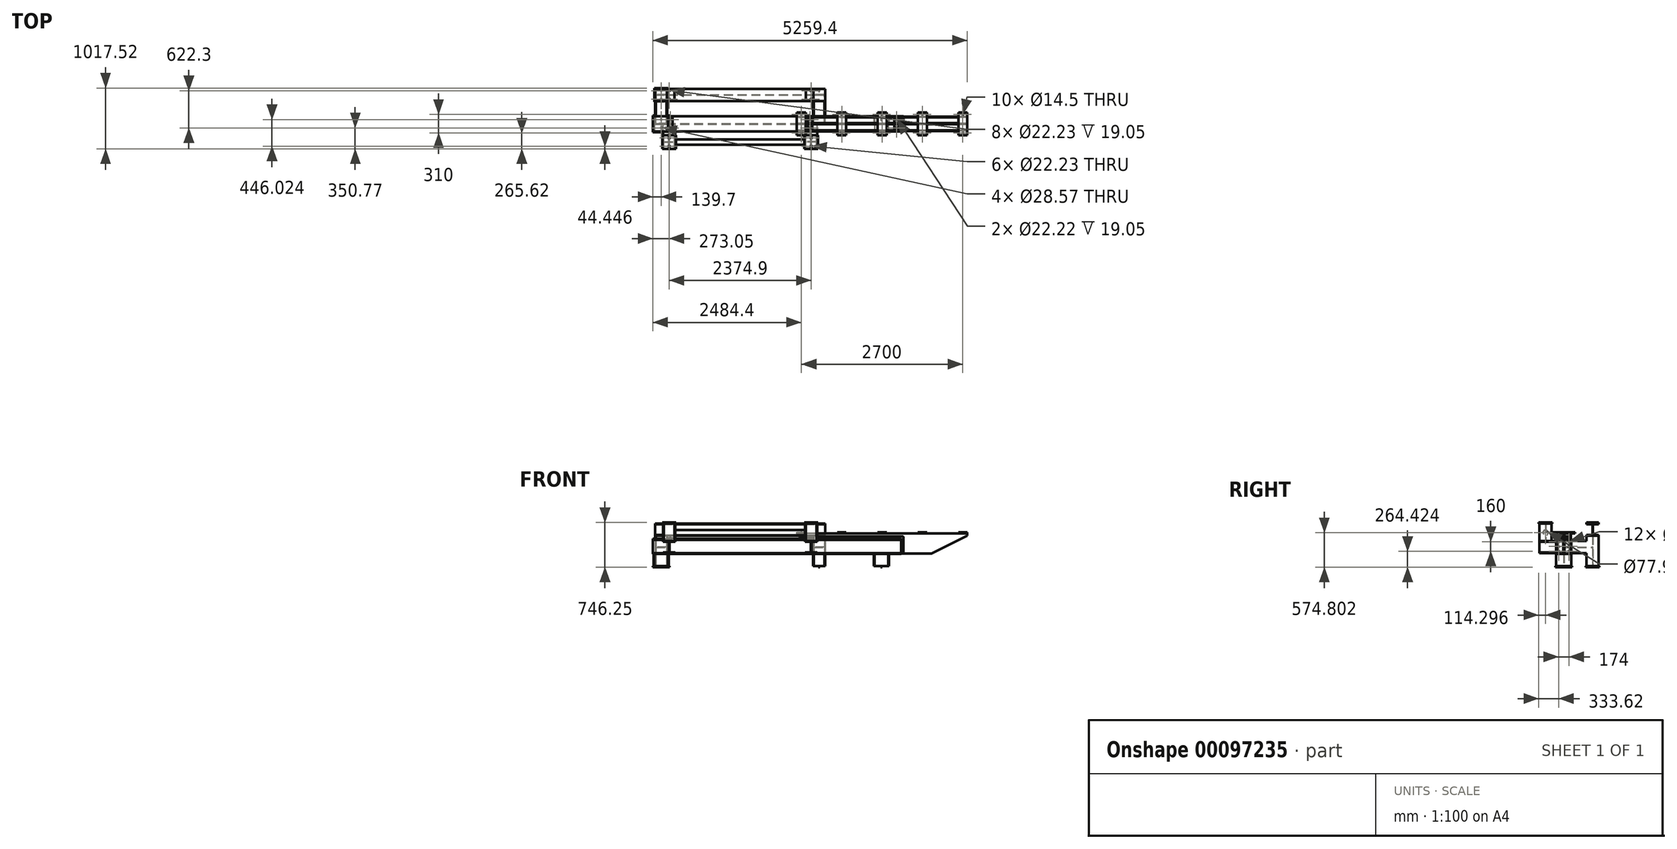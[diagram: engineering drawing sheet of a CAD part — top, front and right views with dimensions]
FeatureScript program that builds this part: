
annotation { "Feature Type Name" : "Feature", "Feature Type Description" : "" }
export const myFeature = defineFeature(function(context is Context, id is Id, definition is map)
    precondition{}
    {
        {
            var Q0;
            Q0=qCreatedBy(makeId("Top.planeOp"),FACE);
            var sketch = newSketch(context, id + "F0", { "sketchPlane" : qUnion([Q0])});
            skLineSegment(sketch, "E0.bottom", {"start": v(-1320.8, 241.3) * mm, "end": v(1320.8, 241.3) * mm, "construction": true});
            skLineSegment(sketch, "E0.top", {"start": v(-1320.8, -241.3) * mm, "end": v(1320.8, -241.3) * mm, "construction": true});
            skLineSegment(sketch, "E0.left", {"start": v(-1320.8, 241.3) * mm, "end": v(-1320.8, -241.3) * mm, "construction": true});
            skLineSegment(sketch, "E0.right", {"start": v(1320.8, 241.3) * mm, "end": v(1320.8, -241.3) * mm, "construction": true});
            skPoint(sketch, "E0.middle", {"position": v(0, 0) * mm});
            skLineSegment(sketch, "E1.bottom", {"start": v(-1435.1, 355.6) * mm, "end": v(-1206.5, 355.6) * mm});
            skLineSegment(sketch, "E1.top", {"start": v(-1435.1, 127) * mm, "end": v(-1206.5, 127) * mm});
            skLineSegment(sketch, "E1.left", {"start": v(-1435.1, 355.6) * mm, "end": v(-1435.1, 127) * mm});
            skLineSegment(sketch, "E1.right", {"start": v(-1206.5, 355.6) * mm, "end": v(-1206.5, 127) * mm});
            skPoint(sketch, "E1.middle", {"position": v(-1320.8, 241.3) * mm});
            skLineSegment(sketch, "E2", {"start": v(0, -413.23) * mm, "end": v(0, 639.03) * mm, "construction": true});
            skLineSegment(sketch, "E3", {"start": v(-1320.8, 355.6) * mm, "end": v(-1320.8, 127) * mm, "construction": true});
            skLineSegment(sketch, "E4", {"start": v(-1435.1, 241.3) * mm, "end": v(-1206.5, 241.3) * mm, "construction": true});
            skLineSegment(sketch, "E5.0", {"start": v(-1435.1, 311.15) * mm, "end": v(-1206.5, 311.15) * mm, "construction": true});
            skCircle(sketch, "E6", {"center": v(-1320.8, 311.15) * mm, "radius": 14.29 * mm});
            skCircle(sketch, "E7.MirrorC", {"center": v(-1320.8, 171.45) * mm, "radius": 14.29 * mm});
            skCircle(sketch, "E8.MirrorC", {"center": v(1320.8, 311.15) * mm, "radius": 14.29 * mm});
            skCircle(sketch, "E9.MirrorC", {"center": v(1320.8, 171.45) * mm, "radius": 14.29 * mm});
            skLineSegment(sketch, "E10.MirrorCS", {"start": v(1435.1, 311.15) * mm, "end": v(1206.5, 311.15) * mm, "construction": true});
            skLineSegment(sketch, "E11.MirrorCS", {"start": v(1435.1, 241.3) * mm, "end": v(1206.5, 241.3) * mm, "construction": true});
            skLineSegment(sketch, "E12.MirrorCS", {"start": v(1320.8, 355.6) * mm, "end": v(1320.8, 127) * mm, "construction": true});
            skLineSegment(sketch, "E13.MirrorCS", {"start": v(1435.1, 355.6) * mm, "end": v(1206.5, 355.6) * mm});
            skPoint(sketch, "E14.MirrorP", {"position": v(1320.8, 241.3) * mm});
            skLineSegment(sketch, "E15.MirrorCS", {"start": v(1206.5, 355.6) * mm, "end": v(1206.5, 127) * mm});
            skLineSegment(sketch, "E16.MirrorCS", {"start": v(1435.1, 127) * mm, "end": v(1206.5, 127) * mm});
            skLineSegment(sketch, "E17.MirrorCS", {"start": v(1435.1, 355.6) * mm, "end": v(1435.1, 127) * mm});
            skLineSegment(sketch, "E18.bottom", {"start": v(-1460.5, -381) * mm, "end": v(-1181.1, -381) * mm});
            skLineSegment(sketch, "E18.top", {"start": v(-1460.5, -101.6) * mm, "end": v(-1181.1, -101.6) * mm});
            skLineSegment(sketch, "E18.left", {"start": v(-1460.5, -381) * mm, "end": v(-1460.5, -101.6) * mm});
            skLineSegment(sketch, "E18.right", {"start": v(-1181.1, -381) * mm, "end": v(-1181.1, -101.6) * mm});
            skPoint(sketch, "E18.middle", {"position": v(-1320.8, -241.3) * mm});
            skLineSegment(sketch, "E19", {"start": v(-1320.8, -241.3) * mm, "end": v(-1460.5, -241.3) * mm, "construction": true});
            skLineSegment(sketch, "E20.0", {"start": v(-1320.8, -171.45) * mm, "end": v(-1460.5, -171.45) * mm, "construction": true});
            skCircle(sketch, "E21", {"center": v(-1320.8, -171.45) * mm, "radius": 14.29 * mm});
            skCircle(sketch, "E22.MirrorC", {"center": v(-1320.8, -311.15) * mm, "radius": 14.29 * mm});
            skLineSegment(sketch, "E23", {"start": v(-1320.8, -638.8) * mm, "end": v(-1320.8, -1011) * mm, "construction": true});
            skPoint(sketch, "E24.orphan", {"position": v(-1320.8, -381) * mm});
            skLineSegment(sketch, "E25.0", {"start": v(0, -638.8) * mm, "end": v(0, -1011) * mm, "construction": true});
            skLineSegment(sketch, "E26.0", {"start": v(1320.8, -638.8) * mm, "end": v(1320.8, -1011) * mm, "construction": true});
            skLineSegment(sketch, "E27.0", {"start": v(2362.2, -638.8) * mm, "end": v(2362.2, -1011) * mm, "construction": true});
            skLineSegment(sketch, "E28", {"start": v(-1320.8, -1011) * mm, "end": v(2362.2, -1011) * mm, "construction": true});
            skLineSegment(sketch, "E29", {"start": v(520.7, -1011) * mm, "end": v(520.7, -1354.57) * mm, "construction": true});
            skCircle(sketch, "E30.MirrorC", {"center": v(2362.2, -171.45) * mm, "radius": 14.29 * mm});
            skCircle(sketch, "E31.MirrorC", {"center": v(2362.2, -311.15) * mm, "radius": 14.29 * mm});
            skLineSegment(sketch, "E32.MirrorCS", {"start": v(2362.2, -171.45) * mm, "end": v(2501.9, -171.45) * mm, "construction": true});
            skLineSegment(sketch, "E33.MirrorCS", {"start": v(2501.9, -101.6) * mm, "end": v(2222.5, -101.6) * mm});
            skLineSegment(sketch, "E34.MirrorCS", {"start": v(2501.9, -381) * mm, "end": v(2222.5, -381) * mm});
            skLineSegment(sketch, "E35.MirrorCS", {"start": v(2362.2, -241.3) * mm, "end": v(2501.9, -241.3) * mm, "construction": true});
            skPoint(sketch, "E36.MirrorP", {"position": v(2362.2, -241.3) * mm});
            skLineSegment(sketch, "E37.MirrorCS", {"start": v(2222.5, -381) * mm, "end": v(2222.5, -101.6) * mm});
            skPoint(sketch, "E38.MirrorP", {"position": v(2362.2, -381) * mm});
            skLineSegment(sketch, "E39.MirrorCS", {"start": v(2501.9, -381) * mm, "end": v(2501.9, -101.6) * mm});
            skSolve(sketch);
        }
        {
            var Q0;
            Q0=makeQuery(id+"F0.imprint","IMPRINT",FACE,{"disambiguationData":[TD([[makeQuery(id+"F0.imprint","IMPRINT",EDGE,{"derivedFrom":sQuery(id+"F0.wireOp",EDGE,"E1.bottom")}),-1.0]])]});
            var Q1;
            Q1=makeQuery(id+"F0.imprint","IMPRINT",FACE,{"disambiguationData":[TD([[makeQuery(id+"F0.imprint","IMPRINT",EDGE,{"derivedFrom":sQuery(id+"F0.wireOp",EDGE,"E8.MirrorC")}),1.0]])]});
            var Q2;
            Q2=makeQuery(id+"F0.imprint","IMPRINT",FACE,{"disambiguationData":[TD([[makeQuery(id+"F0.imprint","IMPRINT",EDGE,{"derivedFrom":sQuery(id+"F0.wireOp",EDGE,"E30.MirrorC")}),1.0]])]});
            var Q3;
            Q3=makeQuery(id+"F0.imprint","IMPRINT",FACE,{"disambiguationData":[TD([[makeQuery(id+"F0.imprint","IMPRINT",EDGE,{"derivedFrom":sQuery(id+"F0.wireOp",EDGE,"E18.bottom")}),1.0]])]});
            extrude(context, id + "F1", {"entities" : qUnion([Q0, Q1, Q2, Q3]), "depth" : 19.05 * mm});
        }
        {
            var Q0;
            Q0=makeQuery(id+"F1.opExtrude","CAP_FACE",FACE,{"disambiguationData":[OSD([sQuery(id+"F0.wireOp",EDGE,"E1.bottom"),sQuery(id+"F0.wireOp",EDGE,"E1.top"),sQuery(id+"F0.wireOp",EDGE,"E1.left"),sQuery(id+"F0.wireOp",EDGE,"E1.right"),sQuery(id+"F0.wireOp",EDGE,"E6"),sQuery(id+"F0.wireOp",EDGE,"E7.MirrorC")])],"isStart":false});
            var sketch = newSketch(context, id + "F2", { "sketchPlane" : qUnion([Q0])});
            skLineSegment(sketch, "E40.0", {"start": v(-1435.1, 241.3) * mm, "end": v(-1206.5, 241.3) * mm, "construction": true});
            skLineSegment(sketch, "E41.0", {"start": v(-1320.8, 355.6) * mm, "end": v(-1320.8, 127) * mm, "construction": true});
            skLineSegment(sketch, "E42.bottom", {"start": v(-1422.4, 342.9) * mm, "end": v(-1411.35, 342.9) * mm});
            skLineSegment(sketch, "E42.top", {"start": v(-1422.4, 139.7) * mm, "end": v(-1411.35, 139.7) * mm});
            skLineSegment(sketch, "E42.left", {"start": v(-1422.4, 342.9) * mm, "end": v(-1422.4, 139.7) * mm});
            skLineSegment(sketch, "E42.right", {"start": v(-1219.2, 342.9) * mm, "end": v(-1219.2, 139.7) * mm, "construction": true});
            skPoint(sketch, "E42.middle", {"position": v(-1320.8, 241.3) * mm});
            skLineSegment(sketch, "E43.0", {"start": v(-1411.35, 342.9) * mm, "end": v(-1411.35, 251.27) * mm});
            skLineSegment(sketch, "E44.trimOffspring", {"start": v(-1405, 237.68) * mm, "end": v(-1320.8, 237.68) * mm});
            skLineSegment(sketch, "E45.MirrorCS", {"start": v(-1405, 244.92) * mm, "end": v(-1320.8, 244.92) * mm});
            skLineSegment(sketch, "E46.trimOffspring", {"start": v(-1411.35, 231.33) * mm, "end": v(-1411.35, 139.7) * mm});
            skPoint(sketch, "E47.visualSharp", {"position": v(-1411.35, 244.92) * mm});
            skArc(sketch, "E47.filletArc", {"start": v(-1411.35, 251.27) * mm, "mid": v(-1409.5, 246.78) * mm, "end": v(-1405, 244.92) * mm});
            skPoint(sketch, "E48.visualSharp", {"position": v(-1411.35, 237.68) * mm});
            skArc(sketch, "E48.filletArc", {"start": v(-1405, 237.68) * mm, "mid": v(-1409.5, 235.82) * mm, "end": v(-1411.35, 231.33) * mm});
            skArc(sketch, "E49.MirrorCS", {"start": v(-1236.6, 237.68) * mm, "mid": v(-1232.1, 235.82) * mm, "end": v(-1230.25, 231.33) * mm});
            skArc(sketch, "E50.MirrorCS", {"start": v(-1230.25, 251.27) * mm, "mid": v(-1232.1, 246.78) * mm, "end": v(-1236.6, 244.92) * mm});
            skPoint(sketch, "E51.MirrorP", {"position": v(-1230.25, 237.68) * mm});
            skPoint(sketch, "E52.MirrorP", {"position": v(-1230.25, 244.92) * mm});
            skLineSegment(sketch, "E53.MirrorCS", {"start": v(-1230.25, 342.9) * mm, "end": v(-1230.25, 251.27) * mm});
            skLineSegment(sketch, "E54.MirrorCS", {"start": v(-1236.6, 237.68) * mm, "end": v(-1320.8, 237.68) * mm});
            skLineSegment(sketch, "E55.MirrorCS", {"start": v(-1236.6, 244.92) * mm, "end": v(-1320.8, 244.92) * mm});
            skLineSegment(sketch, "E56.MirrorCS", {"start": v(-1219.2, 139.7) * mm, "end": v(-1230.25, 139.7) * mm});
            skLineSegment(sketch, "E57.MirrorCS", {"start": v(-1230.25, 231.33) * mm, "end": v(-1230.25, 139.7) * mm});
            skLineSegment(sketch, "E58.MirrorCS", {"start": v(-1219.2, 342.9) * mm, "end": v(-1230.25, 342.9) * mm});
            skLineSegment(sketch, "E59.MirrorCS", {"start": v(-1219.2, 342.9) * mm, "end": v(-1219.2, 139.7) * mm});
            skLineSegment(sketch, "E60.0", {"start": v(0, -413.23) * mm, "end": v(0, 639.03) * mm, "construction": true});
            skArc(sketch, "E61.MirrorCS", {"start": v(1411.35, 251.27) * mm, "mid": v(1409.5, 246.78) * mm, "end": v(1405, 244.92) * mm});
            skArc(sketch, "E62.MirrorCS", {"start": v(1405, 237.68) * mm, "mid": v(1409.5, 235.82) * mm, "end": v(1411.35, 231.33) * mm});
            skLineSegment(sketch, "E63.MirrorCS", {"start": v(1236.6, 244.92) * mm, "end": v(1320.8, 244.92) * mm});
            skArc(sketch, "E64.MirrorCS", {"start": v(1236.6, 237.68) * mm, "mid": v(1232.1, 235.82) * mm, "end": v(1230.25, 231.33) * mm});
            skLineSegment(sketch, "E65.MirrorCS", {"start": v(1422.4, 139.7) * mm, "end": v(1411.35, 139.7) * mm});
            skLineSegment(sketch, "E66.MirrorCS", {"start": v(1422.4, 342.9) * mm, "end": v(1411.35, 342.9) * mm});
            skArc(sketch, "E67.MirrorCS", {"start": v(1230.25, 251.27) * mm, "mid": v(1232.1, 246.78) * mm, "end": v(1236.6, 244.92) * mm});
            skLineSegment(sketch, "E68.MirrorCS", {"start": v(1236.6, 237.68) * mm, "end": v(1320.8, 237.68) * mm});
            skLineSegment(sketch, "E69.MirrorCS", {"start": v(1435.1, 241.3) * mm, "end": v(1206.5, 241.3) * mm, "construction": true});
            skLineSegment(sketch, "E70.MirrorCS", {"start": v(1405, 237.68) * mm, "end": v(1320.8, 237.68) * mm});
            skLineSegment(sketch, "E71.MirrorCS", {"start": v(1219.2, 342.9) * mm, "end": v(1230.25, 342.9) * mm});
            skLineSegment(sketch, "E72.MirrorCS", {"start": v(1219.2, 139.7) * mm, "end": v(1230.25, 139.7) * mm});
            skLineSegment(sketch, "E73.MirrorCS", {"start": v(1411.35, 342.9) * mm, "end": v(1411.35, 251.27) * mm});
            skLineSegment(sketch, "E74.MirrorCS", {"start": v(1405, 244.92) * mm, "end": v(1320.8, 244.92) * mm});
            skLineSegment(sketch, "E75.MirrorCS", {"start": v(1411.35, 231.33) * mm, "end": v(1411.35, 139.7) * mm});
            skPoint(sketch, "E76.MirrorP", {"position": v(1411.35, 237.68) * mm});
            skPoint(sketch, "E77.MirrorP", {"position": v(1320.8, 241.3) * mm});
            skLineSegment(sketch, "E78.MirrorCS", {"start": v(1219.2, 342.9) * mm, "end": v(1219.2, 139.7) * mm, "construction": true});
            skLineSegment(sketch, "E79.MirrorCS", {"start": v(1422.4, 342.9) * mm, "end": v(1422.4, 139.7) * mm});
            skPoint(sketch, "E80.MirrorP", {"position": v(1230.25, 237.68) * mm});
            skLineSegment(sketch, "E81.MirrorCS", {"start": v(1320.8, 355.6) * mm, "end": v(1320.8, 127) * mm, "construction": true});
            skPoint(sketch, "E82.MirrorP", {"position": v(1411.35, 244.92) * mm});
            skLineSegment(sketch, "E83.MirrorCS", {"start": v(1219.2, 342.9) * mm, "end": v(1219.2, 139.7) * mm});
            skLineSegment(sketch, "E84.MirrorCS", {"start": v(1230.25, 231.33) * mm, "end": v(1230.25, 139.7) * mm});
            skLineSegment(sketch, "E85.MirrorCS", {"start": v(1230.25, 342.9) * mm, "end": v(1230.25, 251.27) * mm});
            skPoint(sketch, "E86.MirrorP", {"position": v(1230.25, 244.92) * mm});
            skSolve(sketch);
        }
        {
            var Q0;
            Q0=qSketchRegion(id+"F2",true);
            extrude(context, id + "F3", {"entities" : qUnion([Q0]), "depth" : 504.95 * mm});
        }
        {
            var Q0;
            Q0=makeQuery(id+"F3.opExtrude","SWEPT_FACE",FACE,{"disambiguationData":[OSD([sQuery(id+"F2.wireOp",EDGE,"E79.MirrorCS")])]});
            var sketch = newSketch(context, id + "F4", { "sketchPlane" : qUnion([Q0])});
            skLineSegment(sketch, "E87.bottom", {"start": v(139.7, 524) * mm, "end": v(342.9, 524) * mm});
            skLineSegment(sketch, "E87.top", {"start": v(139.7, 727.2) * mm, "end": v(342.9, 727.2) * mm});
            skLineSegment(sketch, "E87.left", {"start": v(139.7, 524) * mm, "end": v(139.7, 535.05) * mm});
            skLineSegment(sketch, "E87.right", {"start": v(342.9, 524) * mm, "end": v(342.9, 535.05) * mm});
            skLineSegment(sketch, "E88", {"start": v(241.3, 727.2) * mm, "end": v(241.3, 524) * mm, "construction": true});
            skLineSegment(sketch, "E89.0", {"start": v(237.68, 709.8) * mm, "end": v(237.68, 541.4) * mm});
            skLineSegment(sketch, "E90.MirrorCS", {"start": v(244.92, 709.8) * mm, "end": v(244.92, 541.4) * mm});
            skLineSegment(sketch, "E91.0", {"start": v(139.7, 716.15) * mm, "end": v(231.33, 716.15) * mm});
            skLineSegment(sketch, "E92.0", {"start": v(139.7, 535.05) * mm, "end": v(231.33, 535.05) * mm});
            skLineSegment(sketch, "E93.trimOffspring", {"start": v(251.27, 716.15) * mm, "end": v(342.9, 716.15) * mm});
            skLineSegment(sketch, "E94.trimOffspring", {"start": v(251.27, 535.05) * mm, "end": v(342.9, 535.05) * mm});
            skLineSegment(sketch, "E95.trimOffspring", {"start": v(139.7, 716.15) * mm, "end": v(139.7, 727.2) * mm});
            skLineSegment(sketch, "E96.trimOffspring", {"start": v(342.9, 716.15) * mm, "end": v(342.9, 727.2) * mm});
            skPoint(sketch, "E97.newPointB", {"position": v(237.68, 524) * mm});
            skArc(sketch, "E97.filletArc", {"start": v(231.33, 535.05) * mm, "mid": v(235.82, 536.91) * mm, "end": v(237.68, 541.4) * mm});
            skPoint(sketch, "E98.newPointA", {"position": v(244.92, 524) * mm});
            skArc(sketch, "E98.filletArc", {"start": v(244.92, 541.4) * mm, "mid": v(246.78, 536.91) * mm, "end": v(251.27, 535.05) * mm});
            skPoint(sketch, "E99.newPointA", {"position": v(237.68, 727.2) * mm});
            skArc(sketch, "E99.filletArc", {"start": v(237.68, 709.8) * mm, "mid": v(235.82, 714.3) * mm, "end": v(231.33, 716.15) * mm});
            skPoint(sketch, "E100.newPointA", {"position": v(244.92, 727.2) * mm});
            skArc(sketch, "E100.filletArc", {"start": v(251.27, 716.15) * mm, "mid": v(246.78, 714.3) * mm, "end": v(244.92, 709.8) * mm});
            skSolve(sketch);
        }
        {
            var Q0;
            Q0=qSketchRegion(id+"F4",true);
            var Q1;
            Q1=makeQuery(id+"F3.opExtrude","SWEPT_FACE",FACE,{"disambiguationData":[OSD([sQuery(id+"F2.wireOp",EDGE,"E42.left")])]});
            extrude(context, id + "F5", {"entities" : qUnion([Q0]), "endBound" : BoundingType.UP_TO_SURFACE, "oppositeDirection" : true, "endBoundEntityFace" : qUnion([Q1]), "depth" : 25.4 * mm});
        }
        {
            var Q0;
            Q0=makeQuery(id+"F5.opExtrude","SWEPT_FACE",FACE,{"disambiguationData":[OSD([sQuery(id+"F4.wireOp",EDGE,"E87.top")])]});
            var sketch = newSketch(context, id + "F6", { "sketchPlane" : qUnion([Q0])});
            skLineSegment(sketch, "E101.0", {"start": v(0, -413.23) * mm, "end": v(0, 639.03) * mm, "construction": true});
            skLineSegment(sketch, "E102.0", {"start": v(-1187.45, -413.23) * mm, "end": v(-1187.45, 639.03) * mm, "construction": true});
            skLineSegment(sketch, "E103.0", {"start": v(-1225.55, 139.7) * mm, "end": v(-1225.55, 342.9) * mm});
            skLineSegment(sketch, "E104.0", {"start": v(-1098.55, 139.7) * mm, "end": v(-1098.55, 342.9) * mm});
            skLineSegment(sketch, "E105.0", {"start": v(-1422.4, 342.9) * mm, "end": v(1422.4, 342.9) * mm, "construction": true});
            skLineSegment(sketch, "E106.0.0", {"start": v(1225.55, 342.9) * mm, "end": v(-1225.55, 342.9) * mm});
            skLineSegment(sketch, "E106.0.1", {"start": v(-1422.4, 342.9) * mm, "end": v(-1422.4, 139.7) * mm});
            skLineSegment(sketch, "E106.0.2", {"start": v(-1225.55, 139.7) * mm, "end": v(-1098.55, 139.7) * mm});
            skLineSegment(sketch, "E106.0.3", {"start": v(1422.4, 139.7) * mm, "end": v(1422.4, 342.9) * mm});
            skLineSegment(sketch, "E107.trimOffspring", {"start": v(0, 139.7) * mm, "end": v(1225.55, 139.7) * mm});
            skLineSegment(sketch, "E108.0", {"start": v(-1320.8, 241.3) * mm, "end": v(1320.8, 241.3) * mm, "construction": true});
            skLineSegment(sketch, "E109.0", {"start": v(-1320.8, 311.15) * mm, "end": v(1320.8, 311.15) * mm, "construction": true});
            skCircle(sketch, "E110", {"center": v(-1187.45, 311.15) * mm, "radius": 11.11 * mm});
            skCircle(sketch, "E111.MirrorC", {"center": v(-1187.45, 171.45) * mm, "radius": 11.11 * mm});
            skCircle(sketch, "E112.MirrorC", {"center": v(1187.45, 311.15) * mm, "radius": 11.11 * mm});
            skCircle(sketch, "E113.MirrorC", {"center": v(1187.45, 171.45) * mm, "radius": 11.11 * mm});
            skLineSegment(sketch, "E114.MirrorCS", {"start": v(1225.55, 139.7) * mm, "end": v(1098.55, 139.7) * mm});
            skLineSegment(sketch, "E115.MirrorCS", {"start": v(1225.55, 139.7) * mm, "end": v(1225.55, 342.9) * mm});
            skLineSegment(sketch, "E116.MirrorCS", {"start": v(1098.55, 139.7) * mm, "end": v(1098.55, 342.9) * mm});
            skSolve(sketch);
        }
        {
            var Q0;
            Q0=qSketchRegion(id+"F6",true);
            extrude(context, id + "F7", {"entities" : qUnion([Q0]), "operationType" : NewBodyOperationType.ADD, "depth" : 19.05 * mm});
        }
        {
            var Q0;
            Q0=makeQuery(id+"F3.opExtrude","SWEPT_FACE",FACE,{"disambiguationData":[OSD([sQuery(id+"F2.wireOp",EDGE,"E44.trimOffspring"),sQuery(id+"F2.wireOp",EDGE,"E54.MirrorCS")])]});
            var sketch = newSketch(context, id + "F8", { "sketchPlane" : qUnion([Q0])});
            skLineSegment(sketch, "E117.0", {"start": v(-1460.5, 0) * mm, "end": v(-1181.1, 0) * mm, "construction": true});
            skLineSegment(sketch, "E118", {"start": v(-1320.8, 0) * mm, "end": v(-1320.8, 868.41) * mm, "construction": true});
            skLineSegment(sketch, "E119.0", {"start": v(-1422.4, 231.65) * mm, "end": v(-1411.35, 231.65) * mm});
            skLineSegment(sketch, "E120.0", {"start": v(-1422.4, 434.85) * mm, "end": v(-1411.35, 434.85) * mm});
            skLineSegment(sketch, "E121", {"start": v(-1422.4, 434.85) * mm, "end": v(-1422.4, 231.65) * mm});
            skLineSegment(sketch, "E122.0", {"start": v(-1411.35, 434.85) * mm, "end": v(-1411.35, 342.77) * mm});
            skLineSegment(sketch, "E123", {"start": v(-1411.35, 333.25) * mm, "end": v(-1320.8, 333.25) * mm, "construction": true});
            skLineSegment(sketch, "E124.0", {"start": v(-1405, 336.42) * mm, "end": v(-1320.8, 336.42) * mm});
            skLineSegment(sketch, "E125.MirrorCS", {"start": v(-1410.08, 330.07) * mm, "end": v(-1320.8, 330.07) * mm});
            skLineSegment(sketch, "E126.trimOffspring", {"start": v(-1411.35, 328.8) * mm, "end": v(-1411.35, 231.65) * mm});
            skPoint(sketch, "E127.newPointA", {"position": v(-1411.35, 336.42) * mm});
            skArc(sketch, "E127.filletArc", {"start": v(-1411.35, 342.77) * mm, "mid": v(-1409.5, 338.28) * mm, "end": v(-1405, 336.42) * mm});
            skPoint(sketch, "E128.visualSharp", {"position": v(-1411.35, 330.07) * mm});
            skArc(sketch, "E128.filletArc", {"start": v(-1410.08, 330.07) * mm, "mid": v(-1410.98, 329.7) * mm, "end": v(-1411.35, 328.8) * mm});
            skArc(sketch, "E129.MirrorCS", {"start": v(-1231.52, 330.07) * mm, "mid": v(-1230.62, 329.7) * mm, "end": v(-1230.25, 328.8) * mm});
            skArc(sketch, "E130.MirrorCS", {"start": v(-1230.25, 342.77) * mm, "mid": v(-1232.1, 338.28) * mm, "end": v(-1236.6, 336.42) * mm});
            skLineSegment(sketch, "E131.MirrorCS", {"start": v(-1219.2, 231.65) * mm, "end": v(-1230.25, 231.65) * mm});
            skLineSegment(sketch, "E132.MirrorCS", {"start": v(-1219.2, 434.85) * mm, "end": v(-1230.25, 434.85) * mm});
            skPoint(sketch, "E133.MirrorP", {"position": v(-1230.25, 336.42) * mm});
            skPoint(sketch, "E134.MirrorP", {"position": v(-1230.25, 330.07) * mm});
            skLineSegment(sketch, "E135.MirrorCS", {"start": v(-1230.25, 328.8) * mm, "end": v(-1230.25, 231.65) * mm});
            skLineSegment(sketch, "E136.MirrorCS", {"start": v(-1231.52, 330.07) * mm, "end": v(-1320.8, 330.07) * mm});
            skLineSegment(sketch, "E137.MirrorCS", {"start": v(-1219.2, 434.85) * mm, "end": v(-1219.2, 231.65) * mm});
            skLineSegment(sketch, "E138.MirrorCS", {"start": v(-1230.25, 434.85) * mm, "end": v(-1230.25, 342.77) * mm});
            skLineSegment(sketch, "E139.MirrorCS", {"start": v(-1230.25, 333.25) * mm, "end": v(-1320.8, 333.25) * mm, "construction": true});
            skLineSegment(sketch, "E140.MirrorCS", {"start": v(-1236.6, 336.42) * mm, "end": v(-1320.8, 336.42) * mm});
            skLineSegment(sketch, "E141", {"start": v(0, -179.83) * mm, "end": v(0, 965.66) * mm, "construction": true});
            skArc(sketch, "E142.MirrorCS", {"start": v(1411.35, 342.77) * mm, "mid": v(1409.5, 338.28) * mm, "end": v(1405, 336.42) * mm});
            skArc(sketch, "E143.MirrorCS", {"start": v(1410.08, 330.07) * mm, "mid": v(1410.98, 329.7) * mm, "end": v(1411.35, 328.8) * mm});
            skArc(sketch, "E144.MirrorCS", {"start": v(1230.25, 342.77) * mm, "mid": v(1232.1, 338.28) * mm, "end": v(1236.6, 336.42) * mm});
            skArc(sketch, "E145.MirrorCS", {"start": v(1231.52, 330.07) * mm, "mid": v(1230.62, 329.7) * mm, "end": v(1230.25, 328.8) * mm});
            skLineSegment(sketch, "E146.MirrorCS", {"start": v(1411.35, 333.25) * mm, "end": v(1320.8, 333.25) * mm, "construction": true});
            skLineSegment(sketch, "E147.MirrorCS", {"start": v(1219.2, 231.65) * mm, "end": v(1230.25, 231.65) * mm});
            skLineSegment(sketch, "E148.MirrorCS", {"start": v(1219.2, 434.85) * mm, "end": v(1230.25, 434.85) * mm});
            skLineSegment(sketch, "E149.MirrorCS", {"start": v(1422.4, 231.65) * mm, "end": v(1411.35, 231.65) * mm});
            skLineSegment(sketch, "E150.MirrorCS", {"start": v(1422.4, 434.85) * mm, "end": v(1411.35, 434.85) * mm});
            skLineSegment(sketch, "E151.MirrorCS", {"start": v(1405, 336.42) * mm, "end": v(1320.8, 336.42) * mm});
            skLineSegment(sketch, "E152.MirrorCS", {"start": v(1410.08, 330.07) * mm, "end": v(1320.8, 330.07) * mm});
            skLineSegment(sketch, "E153.MirrorCS", {"start": v(1230.25, 333.25) * mm, "end": v(1320.8, 333.25) * mm, "construction": true});
            skLineSegment(sketch, "E154.MirrorCS", {"start": v(1231.52, 330.07) * mm, "end": v(1320.8, 330.07) * mm});
            skLineSegment(sketch, "E155.MirrorCS", {"start": v(1236.6, 336.42) * mm, "end": v(1320.8, 336.42) * mm});
            skLineSegment(sketch, "E156.MirrorCS", {"start": v(1411.35, 328.8) * mm, "end": v(1411.35, 231.65) * mm});
            skPoint(sketch, "E157.MirrorP", {"position": v(1411.35, 330.07) * mm});
            skPoint(sketch, "E158.MirrorP", {"position": v(1411.35, 336.42) * mm});
            skLineSegment(sketch, "E159.MirrorCS", {"start": v(1422.4, 434.85) * mm, "end": v(1422.4, 231.65) * mm});
            skLineSegment(sketch, "E160.MirrorCS", {"start": v(1411.35, 434.85) * mm, "end": v(1411.35, 342.77) * mm});
            skLineSegment(sketch, "E161.MirrorCS", {"start": v(1230.25, 434.85) * mm, "end": v(1230.25, 342.77) * mm});
            skLineSegment(sketch, "E162.MirrorCS", {"start": v(1230.25, 328.8) * mm, "end": v(1230.25, 231.65) * mm});
            skPoint(sketch, "E163.MirrorP", {"position": v(1230.25, 330.07) * mm});
            skPoint(sketch, "E164.MirrorP", {"position": v(1230.25, 336.42) * mm});
            skLineSegment(sketch, "E165.MirrorCS", {"start": v(1219.2, 434.85) * mm, "end": v(1219.2, 231.65) * mm});
            skSolve(sketch);
        }
        {
            var Q0;
            Q0=qSketchRegion(id+"F8",true);
            extrude(context, id + "F9", {"entities" : qUnion([Q0]), "operationType" : NewBodyOperationType.ADD, "depth" : 482.6 * mm});
        }
        {
            var Q0;
            Q0=qCreatedBy(makeId("Right.planeOp"),FACE);
            cPlane(context, id + "F10", {"entities" : qUnion([Q0]), "cplaneType" : CPlaneType.OFFSET, "offset" : 2692.4 * mm, "width" : 152.4 * mm, "height" : 152.4 * mm});
        }
        {
            var Q0;
            Q0=qCreatedBy(id+"F10.planeOp",FACE);
            var sketch = newSketch(context, id + "F11", { "sketchPlane" : qUnion([Q0])});
            skLineSegment(sketch, "E166.0", {"start": v(-381, 19.05) * mm, "end": v(-101.6, 19.05) * mm, "construction": true});
            skLineSegment(sketch, "E167", {"start": v(-241.3, 19.05) * mm, "end": v(-241.3, 468.37) * mm, "construction": true});
            skLineSegment(sketch, "E168.0", {"start": v(-381, 217.42) * mm, "end": v(-101.6, 217.42) * mm, "construction": true});
            skLineSegment(sketch, "E169.bottom", {"start": v(-368.3, 217.42) * mm, "end": v(-114.3, 217.42) * mm});
            skLineSegment(sketch, "E169.top", {"start": v(-368.3, 471.42) * mm, "end": v(-114.3, 471.42) * mm});
            skLineSegment(sketch, "E169.left", {"start": v(-368.3, 217.42) * mm, "end": v(-368.3, 231.65) * mm});
            skLineSegment(sketch, "E169.right", {"start": v(-114.3, 217.42) * mm, "end": v(-114.3, 231.65) * mm});
            skLineSegment(sketch, "E170.0", {"start": v(-368.3, 457.2) * mm, "end": v(-254, 457.2) * mm});
            skLineSegment(sketch, "E171.0", {"start": v(-368.3, 231.65) * mm, "end": v(-254, 231.65) * mm});
            skLineSegment(sketch, "E172.0", {"start": v(-234.95, 238) * mm, "end": v(-234.95, 450.85) * mm});
            skLineSegment(sketch, "E173.MirrorCS", {"start": v(-247.65, 238) * mm, "end": v(-247.65, 450.85) * mm});
            skLineSegment(sketch, "E174.trimOffspring", {"start": v(-368.3, 457.2) * mm, "end": v(-368.3, 471.42) * mm});
            skLineSegment(sketch, "E175.trimOffspring", {"start": v(-114.3, 457.2) * mm, "end": v(-114.3, 471.42) * mm});
            skLineSegment(sketch, "E176.trimOffspring", {"start": v(-228.6, 457.2) * mm, "end": v(-114.3, 457.2) * mm});
            skLineSegment(sketch, "E177.trimOffspring", {"start": v(-228.6, 231.65) * mm, "end": v(-114.3, 231.65) * mm});
            skPoint(sketch, "E178.newPointB", {"position": v(-247.65, 468.37) * mm});
            skArc(sketch, "E178.filletArc", {"start": v(-247.65, 450.85) * mm, "mid": v(-249.5, 455.34) * mm, "end": v(-254, 457.2) * mm});
            skPoint(sketch, "E179.newPointB", {"position": v(-234.95, 468.37) * mm});
            skArc(sketch, "E179.filletArc", {"start": v(-228.6, 457.2) * mm, "mid": v(-233.1, 455.34) * mm, "end": v(-234.95, 450.85) * mm});
            skPoint(sketch, "E180.newPointB", {"position": v(-234.95, 19.05) * mm});
            skArc(sketch, "E180.filletArc", {"start": v(-234.95, 238) * mm, "mid": v(-233.1, 233.5) * mm, "end": v(-228.6, 231.65) * mm});
            skPoint(sketch, "E181.newPointA", {"position": v(-247.65, 19.05) * mm});
            skArc(sketch, "E181.filletArc", {"start": v(-254, 231.65) * mm, "mid": v(-249.5, 233.5) * mm, "end": v(-247.65, 238) * mm});
            skSolve(sketch);
        }
        {
            var Q0;
            Q0=qSketchRegion(id+"F11",true);
            extrude(context, id + "F12", {"entities" : qUnion([Q0]), "oppositeDirection" : true, "depth" : 4152.9 * mm});
        }
        {
            var Q0;
            Q0=makeQuery(id+"F1.opExtrude","CAP_FACE",FACE,{"disambiguationData":[OSD([sQuery(id+"F0.wireOp",EDGE,"E18.bottom"),sQuery(id+"F0.wireOp",EDGE,"E18.top"),sQuery(id+"F0.wireOp",EDGE,"E18.left"),sQuery(id+"F0.wireOp",EDGE,"E18.right"),sQuery(id+"F0.wireOp",EDGE,"E21"),sQuery(id+"F0.wireOp",EDGE,"E22.MirrorC")])],"isStart":false});
            var sketch = newSketch(context, id + "F13", { "sketchPlane" : qUnion([Q0])});
            skLineSegment(sketch, "E182.bottom", {"start": v(-1447.8, -114.3) * mm, "end": v(-1433.58, -114.3) * mm});
            skLineSegment(sketch, "E182.top", {"start": v(-1447.8, -368.3) * mm, "end": v(-1433.58, -368.3) * mm});
            skLineSegment(sketch, "E182.left", {"start": v(-1447.8, -114.3) * mm, "end": v(-1447.8, -368.3) * mm});
            skLineSegment(sketch, "E182.right", {"start": v(-1193.8, -114.3) * mm, "end": v(-1193.8, -368.3) * mm});
            skPoint(sketch, "E182.middle", {"position": v(-1320.8, -241.3) * mm});
            skLineSegment(sketch, "E183.0", {"start": v(-1433.58, -114.3) * mm, "end": v(-1433.58, -236.98) * mm});
            skLineSegment(sketch, "E184.0", {"start": v(-1208.02, -114.3) * mm, "end": v(-1208.02, -236.98) * mm});
            skLineSegment(sketch, "E185.trimOffspring", {"start": v(-1208.02, -114.3) * mm, "end": v(-1193.8, -114.3) * mm});
            skLineSegment(sketch, "E186.trimOffspring", {"start": v(-1208.02, -368.3) * mm, "end": v(-1193.8, -368.3) * mm});
            skLineSegment(sketch, "E187.0", {"start": v(-1208.02, -236.98) * mm, "end": v(-1433.58, -236.98) * mm});
            skLineSegment(sketch, "E188.MirrorCS", {"start": v(-1208.02, -245.62) * mm, "end": v(-1433.58, -245.62) * mm});
            skPoint(sketch, "E189.orphan", {"position": v(-1460.5, -236.98) * mm});
            skPoint(sketch, "E190.orphan", {"position": v(-1460.5, -245.62) * mm});
            skLineSegment(sketch, "E191.trimOffspring", {"start": v(-1433.58, -245.62) * mm, "end": v(-1433.58, -368.3) * mm});
            skPoint(sketch, "E192.orphan", {"position": v(-1320.8, -236.98) * mm});
            skPoint(sketch, "E193.orphan", {"position": v(-1320.8, -245.62) * mm});
            skLineSegment(sketch, "E194.trimOffspring", {"start": v(-1208.02, -245.62) * mm, "end": v(-1208.02, -368.3) * mm});
            skLineSegment(sketch, "E195.MirrorCS", {"start": v(2489.2, -368.3) * mm, "end": v(2474.98, -368.3) * mm});
            skLineSegment(sketch, "E196.MirrorCS", {"start": v(2489.2, -114.3) * mm, "end": v(2474.98, -114.3) * mm});
            skLineSegment(sketch, "E197.MirrorCS", {"start": v(2249.42, -368.3) * mm, "end": v(2235.2, -368.3) * mm});
            skLineSegment(sketch, "E198.MirrorCS", {"start": v(2249.42, -114.3) * mm, "end": v(2235.2, -114.3) * mm});
            skPoint(sketch, "E199.MirrorP", {"position": v(2362.2, -245.62) * mm});
            skPoint(sketch, "E200.MirrorP", {"position": v(2362.2, -236.98) * mm});
            skLineSegment(sketch, "E201.MirrorCS", {"start": v(2249.42, -245.62) * mm, "end": v(2474.98, -245.62) * mm});
            skPoint(sketch, "E202.MirrorP", {"position": v(2501.9, -236.98) * mm});
            skLineSegment(sketch, "E203.MirrorCS", {"start": v(2249.42, -236.98) * mm, "end": v(2474.98, -236.98) * mm});
            skPoint(sketch, "E204.MirrorP", {"position": v(2362.2, -241.3) * mm});
            skPoint(sketch, "E205.MirrorP", {"position": v(2501.9, -245.62) * mm});
            skLineSegment(sketch, "E206.MirrorCS", {"start": v(2249.42, -245.62) * mm, "end": v(2249.42, -368.3) * mm});
            skLineSegment(sketch, "E207.MirrorCS", {"start": v(2474.98, -245.62) * mm, "end": v(2474.98, -368.3) * mm});
            skLineSegment(sketch, "E208.MirrorCS", {"start": v(2249.42, -114.3) * mm, "end": v(2249.42, -236.98) * mm});
            skLineSegment(sketch, "E209.MirrorCS", {"start": v(2474.98, -114.3) * mm, "end": v(2474.98, -236.98) * mm});
            skLineSegment(sketch, "E210.MirrorCS", {"start": v(2235.2, -114.3) * mm, "end": v(2235.2, -368.3) * mm});
            skLineSegment(sketch, "E211.MirrorCS", {"start": v(2489.2, -114.3) * mm, "end": v(2489.2, -368.3) * mm});
            skSolve(sketch);
        }
        {
            var Q0;
            Q0=qSketchRegion(id+"F13",true);
            extrude(context, id + "F14", {"entities" : qUnion([Q0]), "depth" : 198.37 * mm});
        }
        {
            var Q0;
            Q0=makeQuery(id+"F12.opExtrude","SWEPT_FACE",FACE,{"disambiguationData":[OSD([sQuery(id+"F11.wireOp",EDGE,"E169.top")])]});
            var sketch = newSketch(context, id + "F15", { "sketchPlane" : qUnion([Q0])});
            skLineSegment(sketch, "E212.0", {"start": v(-1615.4, -241.3) * mm, "end": v(2831.5, -241.3) * mm, "construction": true});
            skLineSegment(sketch, "E213.0", {"start": v(0, -413.23) * mm, "end": v(0, 639.03) * mm, "construction": true});
            skPoint(sketch, "E214.orphan", {"position": v(-1320.8, -241.3) * mm});
            skLineSegment(sketch, "E215.0", {"start": v(-1168.4, -689.85) * mm, "end": v(-1168.4, 639.03) * mm, "construction": true});
            skLineSegment(sketch, "E216.0", {"start": v(-1130.3, -355.6) * mm, "end": v(-1130.3, -127) * mm});
            skLineSegment(sketch, "E217.0", {"start": v(-1206.5, -127) * mm, "end": v(-1130.3, -127) * mm});
            skLineSegment(sketch, "E218.0", {"start": v(-1615.4, -171.45) * mm, "end": v(2831.5, -171.45) * mm, "construction": true});
            skLineSegment(sketch, "E219.MirrorCS", {"start": v(-1206.5, -355.6) * mm, "end": v(-1130.3, -355.6) * mm});
            skLineSegment(sketch, "E220.MirrorCS", {"start": v(-1206.5, -355.6) * mm, "end": v(-1206.5, -127) * mm});
            skPoint(sketch, "E221.orphan", {"position": v(-1130.3, 639.03) * mm});
            skPoint(sketch, "E222.orphan", {"position": v(-1206.5, 639.03) * mm});
            skPoint(sketch, "E223.orphan", {"position": v(-1615.4, -127) * mm});
            skPoint(sketch, "E224.orphan", {"position": v(-1615.4, -355.6) * mm});
            skPoint(sketch, "E225.orphan", {"position": v(-1206.5, -689.85) * mm});
            skPoint(sketch, "E226.orphan", {"position": v(-1130.3, -689.85) * mm});
            skCircle(sketch, "E227", {"center": v(-1168.4, -171.45) * mm, "radius": 11.11 * mm});
            skCircle(sketch, "E228.MirrorC", {"center": v(-1168.4, -311.15) * mm, "radius": 11.11 * mm});
            skLineSegment(sketch, "E229.1.0.0", {"start": v(1130.3, -355.6) * mm, "end": v(1130.3, -127) * mm});
            skLineSegment(sketch, "E229.1.0.1", {"start": v(1130.3, -355.6) * mm, "end": v(1206.5, -355.6) * mm});
            skLineSegment(sketch, "E229.1.0.2", {"start": v(1130.3, -127) * mm, "end": v(1206.5, -127) * mm});
            skLineSegment(sketch, "E229.1.0.3", {"start": v(1206.5, -355.6) * mm, "end": v(1206.5, -127) * mm});
            skCircle(sketch, "E229.1.0.4", {"center": v(1168.4, -171.45) * mm, "radius": 11.11 * mm});
            skCircle(sketch, "E229.1.0.5", {"center": v(1168.4, -311.15) * mm, "radius": 11.11 * mm});
            skLineSegment(sketch, "E229.direction1", {"start": v(-1206.5, -355.6) * mm, "end": v(1130.3, -355.6) * mm, "construction": true});
            skLineSegment(sketch, "E230.1.0.1", {"start": v(2578.1, -355.6) * mm, "end": v(2578.1, -127) * mm});
            skLineSegment(sketch, "E230.1.0.2", {"start": v(2654.3, -355.6) * mm, "end": v(2654.3, -127) * mm});
            skCircle(sketch, "E230.1.0.3", {"center": v(2616.2, -311.15) * mm, "radius": 11.11 * mm});
            skCircle(sketch, "E230.1.0.4", {"center": v(2616.2, -171.45) * mm, "radius": 11.11 * mm});
            skLineSegment(sketch, "E230.1.0.5", {"start": v(2578.1, -355.6) * mm, "end": v(2654.3, -355.6) * mm});
            skLineSegment(sketch, "E230.1.0.6", {"start": v(2578.1, -127) * mm, "end": v(2654.3, -127) * mm});
            skLineSegment(sketch, "E230.direction1", {"start": v(1320.8, -241.3) * mm, "end": v(2768.6, -241.3) * mm, "construction": true});
            skSolve(sketch);
        }
        {
            var Q0;
            Q0=qSketchRegion(id+"F15",true);
            extrude(context, id + "F16", {"entities" : qUnion([Q0]), "operationType" : NewBodyOperationType.ADD, "depth" : 19.05 * mm});
        }
        {
            var Q0;
            Q0=makeQuery(id+"F12.opExtrude","SWEPT_FACE",FACE,{"disambiguationData":[OSD([sQuery(id+"F11.wireOp",EDGE,"E173.MirrorCS")])]});
            var sketch = newSketch(context, id + "F17", { "sketchPlane" : qUnion([Q0])});
            skLineSegment(sketch, "E231", {"start": v(0, -262.73) * mm, "end": v(0, 1224.7) * mm, "construction": true});
            skLineSegment(sketch, "E232.0", {"start": v(-1320.8, 0) * mm, "end": v(1320.8, 0) * mm, "construction": true});
            skLineSegment(sketch, "E233.0", {"start": v(-1320.8, 231.9) * mm, "end": v(1320.8, 231.9) * mm, "construction": true});
            skLineSegment(sketch, "E234.0", {"start": v(-1187.45, -262.73) * mm, "end": v(-1187.45, 1224.7) * mm, "construction": true});
            skLineSegment(sketch, "E235.0", {"start": v(-1320.8, 333.5) * mm, "end": v(1320.8, 333.5) * mm, "construction": true});
            skLineSegment(sketch, "E236.bottom", {"start": v(-1289.05, 435.1) * mm, "end": v(-1085.85, 435.1) * mm});
            skLineSegment(sketch, "E236.top", {"start": v(-1289.05, 231.9) * mm, "end": v(-1085.85, 231.9) * mm});
            skLineSegment(sketch, "E236.left", {"start": v(-1289.05, 435.1) * mm, "end": v(-1289.05, 424.05) * mm});
            skLineSegment(sketch, "E236.right", {"start": v(-1085.85, 435.1) * mm, "end": v(-1085.85, 424.05) * mm});
            skPoint(sketch, "E236.middle", {"position": v(-1187.45, 333.5) * mm});
            skLineSegment(sketch, "E237.0", {"start": v(-1289.05, 424.05) * mm, "end": v(-1197.36, 424.05) * mm});
            skLineSegment(sketch, "E238.MirrorCS", {"start": v(-1289.05, 242.95) * mm, "end": v(-1197.36, 242.95) * mm});
            skLineSegment(sketch, "E239.0", {"start": v(-1183.9, 249.3) * mm, "end": v(-1183.9, 417.7) * mm});
            skLineSegment(sketch, "E240.MirrorCS", {"start": v(-1191, 249.3) * mm, "end": v(-1191, 417.7) * mm});
            skLineSegment(sketch, "E241", {"start": v(-1177.54, 424.05) * mm, "end": v(-1085.85, 424.05) * mm});
            skLineSegment(sketch, "E242", {"start": v(-1177.54, 242.95) * mm, "end": v(-1085.85, 242.95) * mm});
            skPoint(sketch, "E243.newPointB", {"position": v(-1191, 1224.7) * mm});
            skArc(sketch, "E243.filletArc", {"start": v(-1191, 417.7) * mm, "mid": v(-1192.87, 422.2) * mm, "end": v(-1197.36, 424.05) * mm});
            skPoint(sketch, "E244.newPointA", {"position": v(-1191, -262.73) * mm});
            skArc(sketch, "E244.filletArc", {"start": v(-1197.36, 242.95) * mm, "mid": v(-1192.87, 244.81) * mm, "end": v(-1191, 249.3) * mm});
            skPoint(sketch, "E245.newPointA", {"position": v(-1183.9, -262.73) * mm});
            skArc(sketch, "E245.filletArc", {"start": v(-1183.9, 249.3) * mm, "mid": v(-1182.03, 244.81) * mm, "end": v(-1177.54, 242.95) * mm});
            skPoint(sketch, "E246.newPointB", {"position": v(-1183.9, 1224.7) * mm});
            skArc(sketch, "E246.filletArc", {"start": v(-1177.54, 424.05) * mm, "mid": v(-1182.03, 422.2) * mm, "end": v(-1183.9, 417.7) * mm});
            skLineSegment(sketch, "E247.trimOffspring", {"start": v(-1289.05, 242.95) * mm, "end": v(-1289.05, 231.9) * mm});
            skLineSegment(sketch, "E248.trimOffspring", {"start": v(-1085.85, 242.95) * mm, "end": v(-1085.85, 231.9) * mm});
            skArc(sketch, "E249.MirrorCS", {"start": v(1177.54, 424.05) * mm, "mid": v(1182.03, 422.2) * mm, "end": v(1183.9, 417.7) * mm});
            skArc(sketch, "E250.MirrorCS", {"start": v(1183.9, 249.3) * mm, "mid": v(1182.03, 244.81) * mm, "end": v(1177.54, 242.95) * mm});
            skArc(sketch, "E251.MirrorCS", {"start": v(1197.36, 242.95) * mm, "mid": v(1192.87, 244.81) * mm, "end": v(1191, 249.3) * mm});
            skArc(sketch, "E252.MirrorCS", {"start": v(1191, 417.7) * mm, "mid": v(1192.87, 422.2) * mm, "end": v(1197.36, 424.05) * mm});
            skLineSegment(sketch, "E253.MirrorCS", {"start": v(1085.85, 242.95) * mm, "end": v(1085.85, 231.9) * mm});
            skLineSegment(sketch, "E254.MirrorCS", {"start": v(1183.9, 249.3) * mm, "end": v(1183.9, 417.7) * mm});
            skLineSegment(sketch, "E255.MirrorCS", {"start": v(1289.05, 242.95) * mm, "end": v(1289.05, 231.9) * mm});
            skLineSegment(sketch, "E256.MirrorCS", {"start": v(1085.85, 435.1) * mm, "end": v(1085.85, 424.05) * mm});
            skLineSegment(sketch, "E257.MirrorCS", {"start": v(1289.05, 435.1) * mm, "end": v(1289.05, 424.05) * mm});
            skLineSegment(sketch, "E258.MirrorCS", {"start": v(1289.05, 242.95) * mm, "end": v(1197.36, 242.95) * mm});
            skLineSegment(sketch, "E259.MirrorCS", {"start": v(1289.05, 424.05) * mm, "end": v(1197.36, 424.05) * mm});
            skLineSegment(sketch, "E260.MirrorCS", {"start": v(1289.05, 435.1) * mm, "end": v(1085.85, 435.1) * mm});
            skLineSegment(sketch, "E261.MirrorCS", {"start": v(1177.54, 424.05) * mm, "end": v(1085.85, 424.05) * mm});
            skLineSegment(sketch, "E262.MirrorCS", {"start": v(1289.05, 231.9) * mm, "end": v(1085.85, 231.9) * mm});
            skLineSegment(sketch, "E263.MirrorCS", {"start": v(1177.54, 242.95) * mm, "end": v(1085.85, 242.95) * mm});
            skLineSegment(sketch, "E264.MirrorCS", {"start": v(1191, 249.3) * mm, "end": v(1191, 417.7) * mm});
            skPoint(sketch, "E265.MirrorP", {"position": v(1187.45, 333.5) * mm});
            skSolve(sketch);
        }
        {
            var Q0;
            Q0=qSketchRegion(id+"F17",true);
            extrude(context, id + "F18", {"entities" : qUnion([Q0]), "depth" : 401.57 * mm});
        }
        {
            var Q0;
            Q0=makeQuery(id+"F18.opExtrude","SWEPT_FACE",FACE,{"disambiguationData":[OSD([sQuery(id+"F17.wireOp",EDGE,"E236.bottom")])]});
            var sketch = newSketch(context, id + "F19", { "sketchPlane" : qUnion([Q0])});
            skLineSegment(sketch, "E266.bottom", {"start": v(-1289.05, -649.22) * mm, "end": v(-1278, -649.22) * mm});
            skLineSegment(sketch, "E266.top", {"start": v(-1289.05, -446.02) * mm, "end": v(-1278, -446.02) * mm});
            skLineSegment(sketch, "E266.left", {"start": v(-1289.05, -649.22) * mm, "end": v(-1289.05, -446.02) * mm});
            skLineSegment(sketch, "E266.right", {"start": v(-1085.85, -649.22) * mm, "end": v(-1085.85, -446.02) * mm});
            skLineSegment(sketch, "E267", {"start": v(-1187.45, -446.02) * mm, "end": v(-1187.45, -700.9) * mm, "construction": true});
            skLineSegment(sketch, "E268", {"start": v(-1289.05, -547.62) * mm, "end": v(-1023.84, -547.62) * mm, "construction": true});
            skLineSegment(sketch, "E269.0", {"start": v(-1278, -649.22) * mm, "end": v(-1278, -557.53) * mm});
            skLineSegment(sketch, "E270.MirrorCS", {"start": v(-1096.9, -649.22) * mm, "end": v(-1096.9, -557.53) * mm});
            skLineSegment(sketch, "E271.0", {"start": v(-1271.65, -551.18) * mm, "end": v(-1103.25, -551.18) * mm});
            skLineSegment(sketch, "E272.MirrorCS", {"start": v(-1271.65, -544.07) * mm, "end": v(-1103.25, -544.07) * mm});
            skPoint(sketch, "E273.orphan", {"position": v(-1023.84, -551.18) * mm});
            skPoint(sketch, "E274.orphan", {"position": v(-1023.84, -544.07) * mm});
            skLineSegment(sketch, "E275.trimOffspring", {"start": v(-1096.9, -537.72) * mm, "end": v(-1096.9, -446.02) * mm});
            skPoint(sketch, "E276.orphan", {"position": v(-1289.05, -544.07) * mm});
            skLineSegment(sketch, "E277.trimOffspring", {"start": v(-1278, -537.72) * mm, "end": v(-1278, -446.02) * mm});
            skPoint(sketch, "E278.orphan", {"position": v(-1289.05, -551.18) * mm});
            skLineSegment(sketch, "E279.trimOffspring", {"start": v(-1096.9, -446.02) * mm, "end": v(-1085.85, -446.02) * mm});
            skLineSegment(sketch, "E280.trimOffspring", {"start": v(-1096.9, -649.22) * mm, "end": v(-1085.85, -649.22) * mm});
            skPoint(sketch, "E281.visualSharp", {"position": v(-1278, -544.07) * mm});
            skArc(sketch, "E281.filletArc", {"start": v(-1278, -537.72) * mm, "mid": v(-1276.14, -542.2) * mm, "end": v(-1271.65, -544.07) * mm});
            skPoint(sketch, "E282.visualSharp", {"position": v(-1278, -551.18) * mm});
            skArc(sketch, "E282.filletArc", {"start": v(-1271.65, -551.18) * mm, "mid": v(-1276.14, -553.04) * mm, "end": v(-1278, -557.53) * mm});
            skPoint(sketch, "E283.visualSharp", {"position": v(-1096.9, -551.18) * mm});
            skArc(sketch, "E283.filletArc", {"start": v(-1096.9, -557.53) * mm, "mid": v(-1098.76, -553.04) * mm, "end": v(-1103.25, -551.18) * mm});
            skPoint(sketch, "E284.visualSharp", {"position": v(-1096.9, -544.07) * mm});
            skArc(sketch, "E284.filletArc", {"start": v(-1103.25, -544.07) * mm, "mid": v(-1098.76, -542.2) * mm, "end": v(-1096.9, -537.72) * mm});
            skArc(sketch, "E285.MirrorCS", {"start": v(1271.65, -551.18) * mm, "mid": v(1276.14, -553.04) * mm, "end": v(1278, -557.53) * mm});
            skArc(sketch, "E286.MirrorCS", {"start": v(1278, -537.72) * mm, "mid": v(1276.14, -542.2) * mm, "end": v(1271.65, -544.07) * mm});
            skArc(sketch, "E287.MirrorCS", {"start": v(1096.9, -557.53) * mm, "mid": v(1098.76, -553.04) * mm, "end": v(1103.25, -551.18) * mm});
            skArc(sketch, "E288.MirrorCS", {"start": v(1103.25, -544.07) * mm, "mid": v(1098.76, -542.2) * mm, "end": v(1096.9, -537.72) * mm});
            skLineSegment(sketch, "E289.MirrorCS", {"start": v(1289.05, -547.62) * mm, "end": v(1023.84, -547.62) * mm, "construction": true});
            skLineSegment(sketch, "E290.MirrorCS", {"start": v(1096.9, -649.22) * mm, "end": v(1085.85, -649.22) * mm});
            skLineSegment(sketch, "E291.MirrorCS", {"start": v(1289.05, -649.22) * mm, "end": v(1278, -649.22) * mm});
            skLineSegment(sketch, "E292.MirrorCS", {"start": v(1289.05, -446.02) * mm, "end": v(1278, -446.02) * mm});
            skPoint(sketch, "E293.MirrorP", {"position": v(1096.9, -551.18) * mm});
            skLineSegment(sketch, "E294.MirrorCS", {"start": v(1096.9, -446.02) * mm, "end": v(1085.85, -446.02) * mm});
            skPoint(sketch, "E295.MirrorP", {"position": v(1289.05, -544.07) * mm});
            skPoint(sketch, "E296.MirrorP", {"position": v(1278, -551.18) * mm});
            skLineSegment(sketch, "E297.MirrorCS", {"start": v(1271.65, -551.18) * mm, "end": v(1103.25, -551.18) * mm});
            skLineSegment(sketch, "E298.MirrorCS", {"start": v(1289.05, -649.22) * mm, "end": v(1289.05, -446.02) * mm});
            skPoint(sketch, "E299.MirrorP", {"position": v(1289.05, -551.18) * mm});
            skLineSegment(sketch, "E300.MirrorCS", {"start": v(1085.85, -649.22) * mm, "end": v(1085.85, -446.02) * mm});
            skPoint(sketch, "E301.MirrorP", {"position": v(1278, -544.07) * mm});
            skLineSegment(sketch, "E302.MirrorCS", {"start": v(1096.9, -649.22) * mm, "end": v(1096.9, -557.53) * mm});
            skLineSegment(sketch, "E303.MirrorCS", {"start": v(1278, -537.72) * mm, "end": v(1278, -446.02) * mm});
            skLineSegment(sketch, "E304.MirrorCS", {"start": v(1278, -649.22) * mm, "end": v(1278, -557.53) * mm});
            skLineSegment(sketch, "E305.MirrorCS", {"start": v(1271.65, -544.07) * mm, "end": v(1103.25, -544.07) * mm});
            skPoint(sketch, "E306.MirrorP", {"position": v(1096.9, -544.07) * mm});
            skPoint(sketch, "E307.MirrorP", {"position": v(1023.84, -544.07) * mm});
            skLineSegment(sketch, "E308.MirrorCS", {"start": v(1096.9, -537.72) * mm, "end": v(1096.9, -446.02) * mm});
            skLineSegment(sketch, "E309.MirrorCS", {"start": v(1187.45, -446.02) * mm, "end": v(1187.45, -700.9) * mm, "construction": true});
            skPoint(sketch, "E310.MirrorP", {"position": v(1023.84, -551.18) * mm});
            skSolve(sketch);
        }
        {
            var Q0;
            Q0=qSketchRegion(id+"F19",true);
            extrude(context, id + "F20", {"entities" : qUnion([Q0]), "depth" : 292.1 * mm});
        }
        {
            var Q0;
            Q0=makeQuery(id+"F20.opExtrude","CAP_FACE",FACE,{"disambiguationData":[OSD([sQuery(id+"F19.wireOp",EDGE,"E266.bottom"),sQuery(id+"F19.wireOp",EDGE,"E266.top"),sQuery(id+"F19.wireOp",EDGE,"E266.left"),sQuery(id+"F19.wireOp",EDGE,"E266.right"),sQuery(id+"F19.wireOp",EDGE,"E269.0"),sQuery(id+"F19.wireOp",EDGE,"E270.MirrorCS"),sQuery(id+"F19.wireOp",EDGE,"E271.0"),sQuery(id+"F19.wireOp",EDGE,"E272.MirrorCS"),sQuery(id+"F19.wireOp",EDGE,"E275.trimOffspring"),sQuery(id+"F19.wireOp",EDGE,"E277.trimOffspring"),sQuery(id+"F19.wireOp",EDGE,"E279.trimOffspring"),sQuery(id+"F19.wireOp",EDGE,"E280.trimOffspring"),sQuery(id+"F19.wireOp",EDGE,"E281.filletArc"),sQuery(id+"F19.wireOp",EDGE,"E282.filletArc"),sQuery(id+"F19.wireOp",EDGE,"E283.filletArc"),sQuery(id+"F19.wireOp",EDGE,"E284.filletArc")])],"isStart":false});
            var sketch = newSketch(context, id + "F21", { "sketchPlane" : qUnion([Q0])});
            skLineSegment(sketch, "E311.0", {"start": v(-1289.05, -649.22) * mm, "end": v(-1289.05, -446.02) * mm, "construction": true});
            skLineSegment(sketch, "E312.0", {"start": v(-1085.85, -649.22) * mm, "end": v(-1085.85, -446.02) * mm, "construction": true});
            skLineSegment(sketch, "E313", {"start": v(-1289.05, -547.62) * mm, "end": v(-1085.85, -547.62) * mm, "construction": true});
            skLineSegment(sketch, "E314.bottom", {"start": v(-1301.75, -433.32) * mm, "end": v(-1073.15, -433.32) * mm});
            skLineSegment(sketch, "E314.top", {"start": v(-1301.75, -661.92) * mm, "end": v(-1073.15, -661.92) * mm});
            skLineSegment(sketch, "E314.left", {"start": v(-1301.75, -433.32) * mm, "end": v(-1301.75, -661.92) * mm});
            skLineSegment(sketch, "E314.right", {"start": v(-1073.15, -433.32) * mm, "end": v(-1073.15, -661.92) * mm});
            skPoint(sketch, "E314.middle", {"position": v(-1187.45, -547.62) * mm});
            skLineSegment(sketch, "E315", {"start": v(-1187.45, -433.32) * mm, "end": v(-1187.45, -661.92) * mm, "construction": true});
            skLineSegment(sketch, "E316.0", {"start": v(-1289.05, -477.77) * mm, "end": v(-1085.85, -477.77) * mm, "construction": true});
            skCircle(sketch, "E317", {"center": v(-1187.45, -477.77) * mm, "radius": 11.11 * mm});
            skCircle(sketch, "E318.MirrorC", {"center": v(-1187.45, -617.47) * mm, "radius": 11.11 * mm});
            skCircle(sketch, "E319.MirrorC", {"center": v(1187.45, -617.47) * mm, "radius": 11.11 * mm});
            skCircle(sketch, "E320.MirrorC", {"center": v(1187.45, -477.77) * mm, "radius": 11.11 * mm});
            skLineSegment(sketch, "E321.MirrorCS", {"start": v(1289.05, -477.77) * mm, "end": v(1085.85, -477.77) * mm, "construction": true});
            skLineSegment(sketch, "E322.MirrorCS", {"start": v(1289.05, -547.62) * mm, "end": v(1085.85, -547.62) * mm, "construction": true});
            skLineSegment(sketch, "E323.MirrorCS", {"start": v(1289.05, -649.22) * mm, "end": v(1289.05, -446.02) * mm, "construction": true});
            skLineSegment(sketch, "E324.MirrorCS", {"start": v(1187.45, -433.32) * mm, "end": v(1187.45, -661.92) * mm, "construction": true});
            skPoint(sketch, "E325.MirrorP", {"position": v(1187.45, -547.62) * mm});
            skLineSegment(sketch, "E326.MirrorCS", {"start": v(1073.15, -433.32) * mm, "end": v(1073.15, -661.92) * mm});
            skLineSegment(sketch, "E327.MirrorCS", {"start": v(1301.75, -661.92) * mm, "end": v(1073.15, -661.92) * mm});
            skLineSegment(sketch, "E328.MirrorCS", {"start": v(1301.75, -433.32) * mm, "end": v(1073.15, -433.32) * mm});
            skLineSegment(sketch, "E329.MirrorCS", {"start": v(1085.85, -649.22) * mm, "end": v(1085.85, -446.02) * mm, "construction": true});
            skLineSegment(sketch, "E330.MirrorCS", {"start": v(1301.75, -433.32) * mm, "end": v(1301.75, -661.92) * mm});
            skSolve(sketch);
        }
        {
            var Q0;
            Q0=qSketchRegion(id+"F21",true);
            extrude(context, id + "F22", {"entities" : qUnion([Q0]), "depth" : 19.05 * mm});
        }
        {
            var Q0;
            Q0=makeQuery(id+"F20.opExtrude","SWEPT_FACE",FACE,{"disambiguationData":[OSD([sQuery(id+"F19.wireOp",EDGE,"E266.right")])]});
            var sketch = newSketch(context, id + "F23", { "sketchPlane" : qUnion([Q0])});
            skLineSegment(sketch, "E331.0.0", {"start": v(-649.22, 435.1) * mm, "end": v(-446.02, 435.1) * mm, "construction": true});
            skLineSegment(sketch, "E331.0.1", {"start": v(-446.02, 435.1) * mm, "end": v(-446.02, 727.2) * mm, "construction": true});
            skLineSegment(sketch, "E331.0.2", {"start": v(-446.02, 727.2) * mm, "end": v(-649.22, 727.2) * mm, "construction": true});
            skLineSegment(sketch, "E331.0.3", {"start": v(-649.22, 727.2) * mm, "end": v(-649.22, 435.1) * mm, "construction": true});
            skLineSegment(sketch, "E332.0", {"start": v(-446.02, 574.8) * mm, "end": v(-649.22, 574.8) * mm, "construction": true});
            skLineSegment(sketch, "E333", {"start": v(-547.62, 574.8) * mm, "end": v(-547.62, 602) * mm, "construction": true});
            skCircle(sketch, "E334", {"center": v(-547.62, 574.8) * mm, "radius": 44.45 * mm});
            skCircle(sketch, "E335.0", {"center": v(-547.62, 574.8) * mm, "radius": 38.96 * mm});
            skSolve(sketch);
        }
        {
            var Q0;
            Q0=qSketchRegion(id+"F23",true);
            extrude(context, id + "F24", {"entities" : qUnion([Q0]), "depth" : 2171.7 * mm});
        }
        {
            var Q0;
            Q0=makeQuery(id+"F16.opExtrude","CAP_FACE",FACE,{"disambiguationData":[OSD([sQuery(id+"F15.wireOp",EDGE,"E229.1.0.0"),sQuery(id+"F15.wireOp",EDGE,"E229.1.0.1"),sQuery(id+"F15.wireOp",EDGE,"E229.1.0.2"),sQuery(id+"F15.wireOp",EDGE,"E229.1.0.3"),sQuery(id+"F15.wireOp",EDGE,"E229.1.0.4"),sQuery(id+"F15.wireOp",EDGE,"E229.1.0.5")])],"isStart":false});
            var sketch = newSketch(context, id + "F25", { "sketchPlane" : qUnion([Q0])});
            skLineSegment(sketch, "E336.0.0", {"start": v(1130.3, -127) * mm, "end": v(1130.3, -355.6) * mm});
            skLineSegment(sketch, "E336.0.1", {"start": v(1130.3, -355.6) * mm, "end": v(1206.5, -355.6) * mm});
            skLineSegment(sketch, "E336.0.2", {"start": v(1206.5, -355.6) * mm, "end": v(1206.5, -127) * mm});
            skLineSegment(sketch, "E336.0.3", {"start": v(1206.5, -127) * mm, "end": v(1130.3, -127) * mm});
            skCircle(sketch, "E337.0", {"center": v(1168.4, -311.15) * mm, "radius": 11.11 * mm});
            skCircle(sketch, "E338.0", {"center": v(1168.4, -171.45) * mm, "radius": 11.11 * mm});
            skLineSegment(sketch, "E339.0.0", {"start": v(2578.1, -127) * mm, "end": v(2578.1, -355.6) * mm});
            skLineSegment(sketch, "E339.0.1", {"start": v(2578.1, -355.6) * mm, "end": v(2654.3, -355.6) * mm});
            skLineSegment(sketch, "E339.0.2", {"start": v(2654.3, -355.6) * mm, "end": v(2654.3, -127) * mm});
            skLineSegment(sketch, "E339.0.3", {"start": v(2654.3, -127) * mm, "end": v(2578.1, -127) * mm});
            skCircle(sketch, "E340.0", {"center": v(2616.2, -171.45) * mm, "radius": 11.11 * mm});
            skCircle(sketch, "E341.0", {"center": v(2616.2, -311.15) * mm, "radius": 11.11 * mm});
            skSolve(sketch);
        }
        {
            var Q0;
            Q0 = qSketchRegion(id + "F25", true);
            extrude(context, id + "F26", {"entities" : qUnion([Q0]), "depth" : 19 * mm});
        }
        {
            var Q0;
            {var subQ7=sQuery(id+"F11.wireOp",EDGE,"E174.trimOffspring");var subQ14=sQuery(id+"F11.wireOp",EDGE,"E169.top");Q0=makeQuery(id+"F16.boolean.opBoolean","SPLIT",FACE,{"disambiguationData":[TD([makeQuery(id+"F12.opExtrude","SWEPT_FACE",FACE,{"disambiguationData":[OSD([subQ7])]})])],"derivedFrom":makeQuery(id+"F12.opExtrude","SWEPT_FACE",FACE,{"disambiguationData":[OSD([subQ14])]})});}
            cPlane(context, id + "F27", {"entities" : qUnion([Q0]), "cplaneType" : CPlaneType.OFFSET, "offset" : 108 * mm, "width" : 150 * mm, "height" : 150 * mm});
        }
        {
            var Q0;
            Q0=qCreatedBy(id+"F27.planeOp",FACE);
            var sketch = newSketch(context, id + "F28", { "sketchPlane" : qUnion([Q0])});
            skLineSegment(sketch, "E342.0", {"start": v(2692.4, -1524.13) * mm, "end": v(2692.4, 788.61) * mm, "construction": true});
            skPoint(sketch, "E343.orphan", {"position": v(2692.4, -114.3) * mm});
            skPoint(sketch, "E344.orphan", {"position": v(2692.4, -368.3) * mm});
            skLineSegment(sketch, "E345.0", {"start": v(948.9, -1524.13) * mm, "end": v(948.9, 788.61) * mm, "construction": true});
            skLineSegment(sketch, "E346.0", {"start": v(1023.9, -1524.13) * mm, "end": v(1023.9, 788.61) * mm, "construction": true});
            skLineSegment(sketch, "E347.0", {"start": v(-1460.5, -368.3) * mm, "end": v(-1460.5, -114.3) * mm, "construction": true});
            skLineSegment(sketch, "E348", {"start": v(-1460.5, -241.3) * mm, "end": v(2900.96, -241.3) * mm, "construction": true});
            skPoint(sketch, "E348.endSnap0", {"position": v(-1460.5, -241.3) * mm});
            skLineSegment(sketch, "E349.bottom", {"start": v(948.9, -51.3) * mm, "end": v(1098.9, -51.3) * mm});
            skLineSegment(sketch, "E349.top", {"start": v(948.9, -431.3) * mm, "end": v(1098.9, -431.3) * mm});
            skLineSegment(sketch, "E349.left", {"start": v(948.9, -51.3) * mm, "end": v(948.9, -431.3) * mm});
            skLineSegment(sketch, "E349.right", {"start": v(1098.9, -51.3) * mm, "end": v(1098.9, -431.3) * mm});
            skPoint(sketch, "E349.middle", {"position": v(1023.9, -241.3) * mm});
            skLineSegment(sketch, "E350.0", {"start": v(-1460.5, -86.3) * mm, "end": v(2900.96, -86.3) * mm, "construction": true});
            skCircle(sketch, "E351", {"center": v(1023.9, -86.3) * mm, "radius": 7.25 * mm});
            skCircle(sketch, "E352.MirrorC", {"center": v(1023.9, -396.3) * mm, "radius": 7.25 * mm});
            skPoint(sketch, "E353.1.0.0", {"position": v(1698.9, -241.3) * mm});
            skLineSegment(sketch, "E353.1.0.1", {"start": v(1773.9, -51.3) * mm, "end": v(1773.9, -431.3) * mm});
            skLineSegment(sketch, "E353.1.0.2", {"start": v(1623.9, -51.3) * mm, "end": v(1773.9, -51.3) * mm});
            skLineSegment(sketch, "E353.1.0.3", {"start": v(1623.9, -431.3) * mm, "end": v(1773.9, -431.3) * mm});
            skLineSegment(sketch, "E353.1.0.4", {"start": v(1623.9, -51.3) * mm, "end": v(1623.9, -431.3) * mm});
            skCircle(sketch, "E353.1.0.5", {"center": v(1698.9, -396.3) * mm, "radius": 7.25 * mm});
            skCircle(sketch, "E353.1.0.6", {"center": v(1698.9, -86.3) * mm, "radius": 7.25 * mm});
            skPoint(sketch, "E353.2.0.0", {"position": v(2373.9, -241.3) * mm});
            skLineSegment(sketch, "E353.2.0.1", {"start": v(2448.9, -51.3) * mm, "end": v(2448.9, -431.3) * mm});
            skLineSegment(sketch, "E353.2.0.2", {"start": v(2298.9, -51.3) * mm, "end": v(2448.9, -51.3) * mm});
            skLineSegment(sketch, "E353.2.0.3", {"start": v(2298.9, -431.3) * mm, "end": v(2448.9, -431.3) * mm});
            skLineSegment(sketch, "E353.2.0.4", {"start": v(2298.9, -51.3) * mm, "end": v(2298.9, -431.3) * mm});
            skCircle(sketch, "E353.2.0.5", {"center": v(2373.9, -396.3) * mm, "radius": 7.25 * mm});
            skCircle(sketch, "E353.2.0.6", {"center": v(2373.9, -86.3) * mm, "radius": 7.25 * mm});
            skLineSegment(sketch, "E353.direction1", {"start": v(1023.9, -241.3) * mm, "end": v(1698.9, -241.3) * mm, "construction": true});
            skPoint(sketch, "E354.0.3.0", {"position": v(3048.9, -241.3) * mm});
            skLineSegment(sketch, "E354.1.3.0", {"start": v(3123.9, -51.3) * mm, "end": v(3123.9, -431.3) * mm});
            skLineSegment(sketch, "E354.4.3.0", {"start": v(2973.9, -51.3) * mm, "end": v(3123.9, -51.3) * mm});
            skLineSegment(sketch, "E354.7.3.0", {"start": v(2973.9, -431.3) * mm, "end": v(3123.9, -431.3) * mm});
            skLineSegment(sketch, "E354.10.3.0", {"start": v(2973.9, -51.3) * mm, "end": v(2973.9, -431.3) * mm});
            skCircle(sketch, "E354.13.3.0", {"center": v(3048.9, -396.3) * mm, "radius": 7.25 * mm});
            skCircle(sketch, "E354.15.3.0", {"center": v(3048.9, -86.3) * mm, "radius": 7.25 * mm});
            skPoint(sketch, "E354.0.4.0", {"position": v(3723.9, -241.3) * mm});
            skLineSegment(sketch, "E354.1.4.0", {"start": v(3798.9, -51.3) * mm, "end": v(3798.9, -431.3) * mm});
            skLineSegment(sketch, "E354.4.4.0", {"start": v(3648.9, -51.3) * mm, "end": v(3798.9, -51.3) * mm});
            skLineSegment(sketch, "E354.7.4.0", {"start": v(3648.9, -431.3) * mm, "end": v(3798.9, -431.3) * mm});
            skLineSegment(sketch, "E354.10.4.0", {"start": v(3648.9, -51.3) * mm, "end": v(3648.9, -431.3) * mm});
            skCircle(sketch, "E354.13.4.0", {"center": v(3723.9, -396.3) * mm, "radius": 7.25 * mm});
            skCircle(sketch, "E354.15.4.0", {"center": v(3723.9, -86.3) * mm, "radius": 7.25 * mm});
            skSolve(sketch);
        }
        {
            var Q0;
            Q0 = qSketchRegion(id + "F28", true);
            extrude(context, id + "F29", {"entities" : qUnion([Q0]), "oppositeDirection" : true, "depth" : 19 * mm});
        }
        {
            var Q0;
            Q0=makeQuery(id+"F26.opExtrude","SWEPT_FACE",FACE,{"disambiguationData":[OSD([sQuery(id+"F25.wireOp",EDGE,"E336.0.1")])]});
            var Q1;
            Q1=makeQuery(id+"F26.opExtrude","SWEPT_FACE",FACE,{"disambiguationData":[OSD([sQuery(id+"F25.wireOp",EDGE,"E336.0.3")])]});
            cPlane(context, id + "F30", {"entities" : qUnion([Q0, Q1]), "cplaneType" : CPlaneType.MID_PLANE, "offset" : 150 * mm, "width" : 150 * mm, "height" : 150 * mm});
        }
        {
            var Q0;
            Q0=qCreatedBy(id+"F10.planeOp",FACE);
            var sketch = newSketch(context, id + "F31", { "sketchPlane" : qUnion([Q0])});
            skLineSegment(sketch, "E355.0.0", {"start": v(-368.3, 231.65) * mm, "end": v(-368.3, 217.42) * mm, "construction": true});
            skLineSegment(sketch, "E355.0.1", {"start": v(-368.3, 217.42) * mm, "end": v(-114.3, 217.42) * mm, "construction": true});
            skLineSegment(sketch, "E355.0.2", {"start": v(-114.3, 217.42) * mm, "end": v(-114.3, 231.65) * mm, "construction": true});
            skLineSegment(sketch, "E355.0.3", {"start": v(-114.3, 231.65) * mm, "end": v(-228.6, 231.65) * mm, "construction": true});
            skArc(sketch, "E355.0.4", {"start": v(-228.6, 231.65) * mm, "mid": v(-233.1, 233.5) * mm, "end": v(-234.95, 238) * mm, "construction": true});
            skLineSegment(sketch, "E355.0.5", {"start": v(-234.95, 238) * mm, "end": v(-234.95, 450.85) * mm, "construction": true});
            skArc(sketch, "E355.0.6", {"start": v(-234.95, 450.85) * mm, "mid": v(-233.1, 455.34) * mm, "end": v(-228.6, 457.2) * mm, "construction": true});
            skLineSegment(sketch, "E355.0.7", {"start": v(-228.6, 457.2) * mm, "end": v(-114.3, 457.2) * mm, "construction": true});
            skLineSegment(sketch, "E355.0.8", {"start": v(-114.3, 457.2) * mm, "end": v(-114.3, 471.42) * mm, "construction": true});
            skLineSegment(sketch, "E355.0.9", {"start": v(-114.3, 471.42) * mm, "end": v(-368.3, 471.42) * mm, "construction": true});
            skLineSegment(sketch, "E355.0.10", {"start": v(-368.3, 471.42) * mm, "end": v(-368.3, 457.2) * mm, "construction": true});
            skLineSegment(sketch, "E355.0.11", {"start": v(-368.3, 457.2) * mm, "end": v(-254, 457.2) * mm, "construction": true});
            skArc(sketch, "E355.0.12", {"start": v(-254, 457.2) * mm, "mid": v(-249.5, 455.34) * mm, "end": v(-247.65, 450.85) * mm, "construction": true});
            skLineSegment(sketch, "E355.0.13", {"start": v(-247.65, 450.85) * mm, "end": v(-247.65, 238) * mm, "construction": true});
            skArc(sketch, "E355.0.14", {"start": v(-247.65, 238) * mm, "mid": v(-249.5, 233.5) * mm, "end": v(-254, 231.65) * mm, "construction": true});
            skLineSegment(sketch, "E355.0.15", {"start": v(-254, 231.65) * mm, "end": v(-368.3, 231.65) * mm, "construction": true});
            skLineSegment(sketch, "E356.bottom", {"start": v(-368.3, 464.31) * mm, "end": v(-114.3, 464.31) * mm});
            skLineSegment(sketch, "E356.top", {"start": v(-368.3, 224.54) * mm, "end": v(-114.3, 224.54) * mm});
            skLineSegment(sketch, "E356.left", {"start": v(-368.3, 464.31) * mm, "end": v(-368.3, 224.54) * mm});
            skLineSegment(sketch, "E356.right", {"start": v(-114.3, 464.31) * mm, "end": v(-114.3, 224.54) * mm});
            skLineSegment(sketch, "E357", {"start": v(-368.3, 344.42) * mm, "end": v(-114.3, 344.42) * mm, "construction": true});
            skLineSegment(sketch, "E358.0", {"start": v(-368.3, 424.42) * mm, "end": v(-114.3, 424.42) * mm, "construction": true});
            skLineSegment(sketch, "E359.0", {"start": v(-328.3, 464.31) * mm, "end": v(-328.3, 224.54) * mm, "construction": true});
            skLineSegment(sketch, "E360.MirrorCS", {"start": v(-368.3, 264.42) * mm, "end": v(-114.3, 264.42) * mm, "construction": true});
            skCircle(sketch, "E361", {"center": v(-328.3, 424.42) * mm, "radius": 10 * mm});
            skCircle(sketch, "E362", {"center": v(-328.3, 344.42) * mm, "radius": 10 * mm});
            skCircle(sketch, "E363", {"center": v(-328.3, 264.42) * mm, "radius": 10 * mm});
            skLineSegment(sketch, "E364", {"start": v(-241.3, 471.42) * mm, "end": v(-241.3, 217.42) * mm, "construction": true});
            skCircle(sketch, "E365.MirrorC", {"center": v(-154.3, 264.42) * mm, "radius": 10 * mm});
            skCircle(sketch, "E366.MirrorC", {"center": v(-154.3, 424.42) * mm, "radius": 10 * mm});
            skCircle(sketch, "E367.MirrorC", {"center": v(-154.3, 344.42) * mm, "radius": 10 * mm});
            skSolve(sketch);
        }
        {
            var Q0;
            Q0 = qSketchRegion(id + "F31", true);
            extrude(context, id + "F32", {"entities" : qUnion([Q0]), "depth" : 19 * mm});
        }
        {
            var Q0;
            Q0=makeQuery(id+"F32.opExtrude","CAP_FACE",FACE,{"disambiguationData":[OSD([sQuery(id+"F31.wireOp",EDGE,"E356.bottom"),sQuery(id+"F31.wireOp",EDGE,"E356.top"),sQuery(id+"F31.wireOp",EDGE,"E356.left"),sQuery(id+"F31.wireOp",EDGE,"E356.right"),sQuery(id+"F31.wireOp",EDGE,"E361"),sQuery(id+"F31.wireOp",EDGE,"E362"),sQuery(id+"F31.wireOp",EDGE,"E363"),sQuery(id+"F31.wireOp",EDGE,"E365.MirrorC"),sQuery(id+"F31.wireOp",EDGE,"E366.MirrorC"),sQuery(id+"F31.wireOp",EDGE,"E367.MirrorC")])],"isStart":false});
            var sketch = newSketch(context, id + "F33", { "sketchPlane" : qUnion([Q0])});
            skLineSegment(sketch, "E368.0.0", {"start": v(-114.3, 464.31) * mm, "end": v(-368.3, 464.31) * mm});
            skLineSegment(sketch, "E368.0.1", {"start": v(-368.3, 464.31) * mm, "end": v(-368.3, 224.54) * mm});
            skLineSegment(sketch, "E368.0.2", {"start": v(-368.3, 224.54) * mm, "end": v(-114.3, 224.54) * mm});
            skLineSegment(sketch, "E368.0.3", {"start": v(-114.3, 224.54) * mm, "end": v(-114.3, 464.31) * mm});
            skCircle(sketch, "E369.0", {"center": v(-328.3, 424.42) * mm, "radius": 10 * mm});
            skCircle(sketch, "E370.0", {"center": v(-328.3, 344.42) * mm, "radius": 10 * mm});
            skCircle(sketch, "E371.0", {"center": v(-328.3, 264.42) * mm, "radius": 10 * mm});
            skCircle(sketch, "E372.0", {"center": v(-154.3, 264.42) * mm, "radius": 10 * mm});
            skCircle(sketch, "E373.0", {"center": v(-154.3, 344.42) * mm, "radius": 10 * mm});
            skCircle(sketch, "E374.0", {"center": v(-154.3, 424.42) * mm, "radius": 10 * mm});
            skSolve(sketch);
        }
        {
            var Q0;
            Q0 = qSketchRegion(id + "F33", true);
            extrude(context, id + "F34", {"entities" : qUnion([Q0]), "depth" : 19 * mm});
        }
        {
            var Q0;
            Q0=qCreatedBy(id+"F30.planeOp",FACE);
            var sketch = newSketch(context, id + "F35", { "sketchPlane" : qUnion([Q0])});
            skLineSegment(sketch, "E375.0", {"start": v(948.9, 560.42) * mm, "end": v(1098.9, 560.42) * mm, "construction": true});
            skLineSegment(sketch, "E376.0", {"start": v(2973.9, 560.42) * mm, "end": v(3123.9, 560.42) * mm, "construction": true});
            skLineSegment(sketch, "E377.0", {"start": v(3648.9, 560.42) * mm, "end": v(3798.9, 560.42) * mm, "construction": true});
            skLineSegment(sketch, "E378.0", {"start": v(2730.4, 464.31) * mm, "end": v(2730.4, 224.54) * mm, "construction": true});
            skLineSegment(sketch, "E379", {"start": v(948.9, 560.42) * mm, "end": v(3798.9, 560.42) * mm});
            skLineSegment(sketch, "E380.0", {"start": v(1130.3, 509.47) * mm, "end": v(1206.5, 509.47) * mm, "construction": true});
            skLineSegment(sketch, "E381", {"start": v(3798.9, 560.42) * mm, "end": v(3798.9, 224.54) * mm});
            skLineSegment(sketch, "E382", {"start": v(3798.9, 224.54) * mm, "end": v(2730.4, 224.54) * mm});
            skLineSegment(sketch, "E383", {"start": v(948.9, 560.42) * mm, "end": v(948.9, 509.47) * mm});
            skLineSegment(sketch, "E384", {"start": v(948.9, 509.47) * mm, "end": v(2720.4, 509.47) * mm});
            skLineSegment(sketch, "E385", {"start": v(2730.4, 499.47) * mm, "end": v(2730.4, 464.31) * mm});
            skLineSegment(sketch, "E386", {"start": v(2730.4, 464.31) * mm, "end": v(2730.4, 224.54) * mm});
            skPoint(sketch, "E387.visualSharp", {"position": v(2730.4, 509.47) * mm});
            skArc(sketch, "E387.filletArc", {"start": v(2730.4, 499.47) * mm, "mid": v(2727.47, 506.55) * mm, "end": v(2720.4, 509.47) * mm});
            skSolve(sketch);
        }
        {
            var Q0;
            Q0 = qSketchRegion(id + "F35", true);
            extrude(context, id + "F36", {"entities" : qUnion([Q0]), "endBound" : BoundingType.SYMMETRIC, "depth" : 19 * mm});
        }
        {
            var Q0;
            Q0=makeQuery(id+"F26.opExtrude","SWEPT_FACE",FACE,{"disambiguationData":[OSD([sQuery(id+"F25.wireOp",EDGE,"E336.0.1")])]});
            var sketch = newSketch(context, id + "F37", { "sketchPlane" : qUnion([Q0])});
            skLineSegment(sketch, "E388.0.0", {"start": v(3798.9, 560.42) * mm, "end": v(948.9, 560.42) * mm});
            skLineSegment(sketch, "E388.0.1", {"start": v(948.9, 560.42) * mm, "end": v(948.9, 509.47) * mm});
            skLineSegment(sketch, "E388.0.2", {"start": v(948.9, 509.47) * mm, "end": v(2720.4, 509.47) * mm});
            skArc(sketch, "E388.0.3", {"start": v(2720.4, 509.47) * mm, "mid": v(2727.47, 506.55) * mm, "end": v(2730.4, 499.47) * mm});
            skLineSegment(sketch, "E388.0.4", {"start": v(2730.4, 499.47) * mm, "end": v(2730.4, 224.54) * mm});
            skLineSegment(sketch, "E388.0.5", {"start": v(2730.4, 224.54) * mm, "end": v(3798.9, 224.54) * mm});
            skLineSegment(sketch, "E388.0.6", {"start": v(3798.9, 224.54) * mm, "end": v(3798.9, 560.42) * mm});
            skSolve(sketch);
        }
        {
            var Q0;
            Q0 = qSketchRegion(id + "F37", true);
            extrude(context, id + "F38", {"entities" : qUnion([Q0]), "endBound" : BoundingType.SYMMETRIC, "depth" : 12.5 * mm});
        }
        {
            var Q0;
            Q0=makeQuery(id+"F36.opExtrude","SWEPT_EDGE",EDGE,{"disambiguationData":[OSD([sQuery(id+"F35.wireOp",EDGE,"E381"),sQuery(id+"F35.wireOp",EDGE,"E382")])]});
            var Q1;
            Q1=makeQuery(id+"F38.opExtrude","SWEPT_EDGE",EDGE,{"disambiguationData":[OSD([sQuery(id+"F37.wireOp",EDGE,"E388.0.5"),sQuery(id+"F37.wireOp",EDGE,"E388.0.6")])]});
            chamfer(context, id + "F39", {"entities" : qUnion([Q0, Q1]), "chamferType" : ChamferType.TWO_OFFSETS, "width1" : 300 * mm, "oppositeDirection" : false, "width2" : 600 * mm, "tangentPropagation" : true});
        }
        {
            var Q0;
            Q0=makeQuery(id+"F38.opExtrude","SWEPT_BODY",BODY,{"disambiguationData":[OSD([sQuery(id+"F37.wireOp",EDGE,"E388.0.0"),sQuery(id+"F37.wireOp",EDGE,"E388.0.1"),sQuery(id+"F37.wireOp",EDGE,"E388.0.2"),sQuery(id+"F37.wireOp",EDGE,"E388.0.3"),sQuery(id+"F37.wireOp",EDGE,"E388.0.4"),sQuery(id+"F37.wireOp",EDGE,"E388.0.5"),sQuery(id+"F37.wireOp",EDGE,"E388.0.6")])]});
            var Q1;
            Q1=qCreatedBy(id+"F30.planeOp",FACE);
            mirror(context, id + "F40", {"entities" : qUnion([Q0]), "mirrorPlane" : qUnion([Q1])});
        }
        {
            var Q0;
            Q0=makeQuery(id+"F36.opExtrude","SWEPT_EDGE",EDGE,{"disambiguationData":[OSD([sQuery(id+"F35.wireOp",EDGE,"E383"),sQuery(id+"F35.wireOp",EDGE,"E384")])]});
            var Q1;
            Q1=makeQuery(id+"F40.opPattern","COPY",EDGE,{"derivedFrom":makeQuery(id+"F38.opExtrude","SWEPT_EDGE",EDGE,{"disambiguationData":[OSD([sQuery(id+"F37.wireOp",EDGE,"E388.0.1"),sQuery(id+"F37.wireOp",EDGE,"E388.0.2")])]}),"instanceName":"1"});
            var Q2;
            Q2=makeQuery(id+"F38.opExtrude","SWEPT_EDGE",EDGE,{"disambiguationData":[OSD([sQuery(id+"F37.wireOp",EDGE,"E388.0.1"),sQuery(id+"F37.wireOp",EDGE,"E388.0.2")])]});
            chamfer(context, id + "F41", {"entities" : qUnion([Q0, Q1, Q2]), "width" : 40 * mm, "tangentPropagation" : true});
        }
    });
